FCSTD DOCUMENT  (FreeCAD 0.20R29603 (Git))
Label: Tutorial
License: All rights reserved
LicenseURL: http://en.wikipedia.org/wiki/All_rights_reserved
objects: Sketcher::SketchObject×2, PartDesign::Body×1
note: 3 computed .brp shape members not serialized (recipe doc carries the construction recipe); baked Part::Feature solids carry a one-line shape summary decoded from their .brp

FEATURE [Sketcher::SketchObject] Sketch
  FullyConstrained = true
  MapMode = 5
  Placement = pos=(0,0,0) rot=(0.57735,0.57735,0.57735;2.0944rad)
  Support = -> [YZ_Plane]
FEATURE [Sketcher::SketchObject] Sketch001
  FullyConstrained = true
  MapMode = 5
  Placement = pos=(0,0,0) rot=(0.57735,0.57735,0.57735;2.0944rad)
  Support = -> [YZ_Plane]
  sketch-geometry (7):
    g0: LineSegment StartX=0 StartY=0 StartZ=0 EndX=69.732 EndY=149.541 EndZ=0
    g1: LineSegment StartX=57.0112 StartY=122.261 StartZ=0 EndX=600.796 EndY=-131.31 EndZ=0
    g2: LineSegment StartX=519.228 StartY=-93.2744 StartZ=0 EndX=667.5 EndY=-344.3 EndZ=0
    g3: LineSegment StartX=667.5 StartY=-344.3 StartZ=0 EndX=667.5 EndY=-512.3 EndZ=0
    g4: LineSegment StartX=667.5 StartY=-512.3 StartZ=0 EndX=334.8 EndY=-481.436 EndZ=0
    g5: LineSegment StartX=334.8 StartY=-481.436 StartZ=0 EndX=168.99 EndY=-189.91 EndZ=0
    g6: LineSegment StartX=168.99 StartY=-189.91 StartZ=0 EndX=27.4702 EndY=58.91 EndZ=0
  constraints (23):
    c: Coincident(g0,g-1)
    c: Distance(g0) = 165
    c: Angle(g0,g-2) = 0.436332
    c: PointOnObject(g1,g0)
    c: Perpendicular(g0,g1)
    c: Distance(g0,g1) = 30.1
    c: Distance(g1) = 600
    c: PointOnObject(g2,g1)
    c: Coincident(g3,g2)
    c: Vertical(g3)
    c: Coincident(g4,g3)
    c: Coincident(g5,g4)
    c: Coincident(g6,g5)
    c: PointOnObject(g6,g0)
    c: Parallel(g5,g6)
    c: Distance(g3,g-1) = 512.3
    c: Distance(g2,g0) = 510
    c: Distance(g3) = 168
    c: Angle(g3,g4) = 1.47829
    c: Distance(g4,g-2) = 334.8
    c: Distance(g3,g-2) = 667.5
    c: Distance(g6) = 286.25
    c: Distance(g6,g0) = 100
FEATURE [PartDesign::Body] Body
  Group = -> [Sketch,Sketch001]
  Origin = -> Origin
